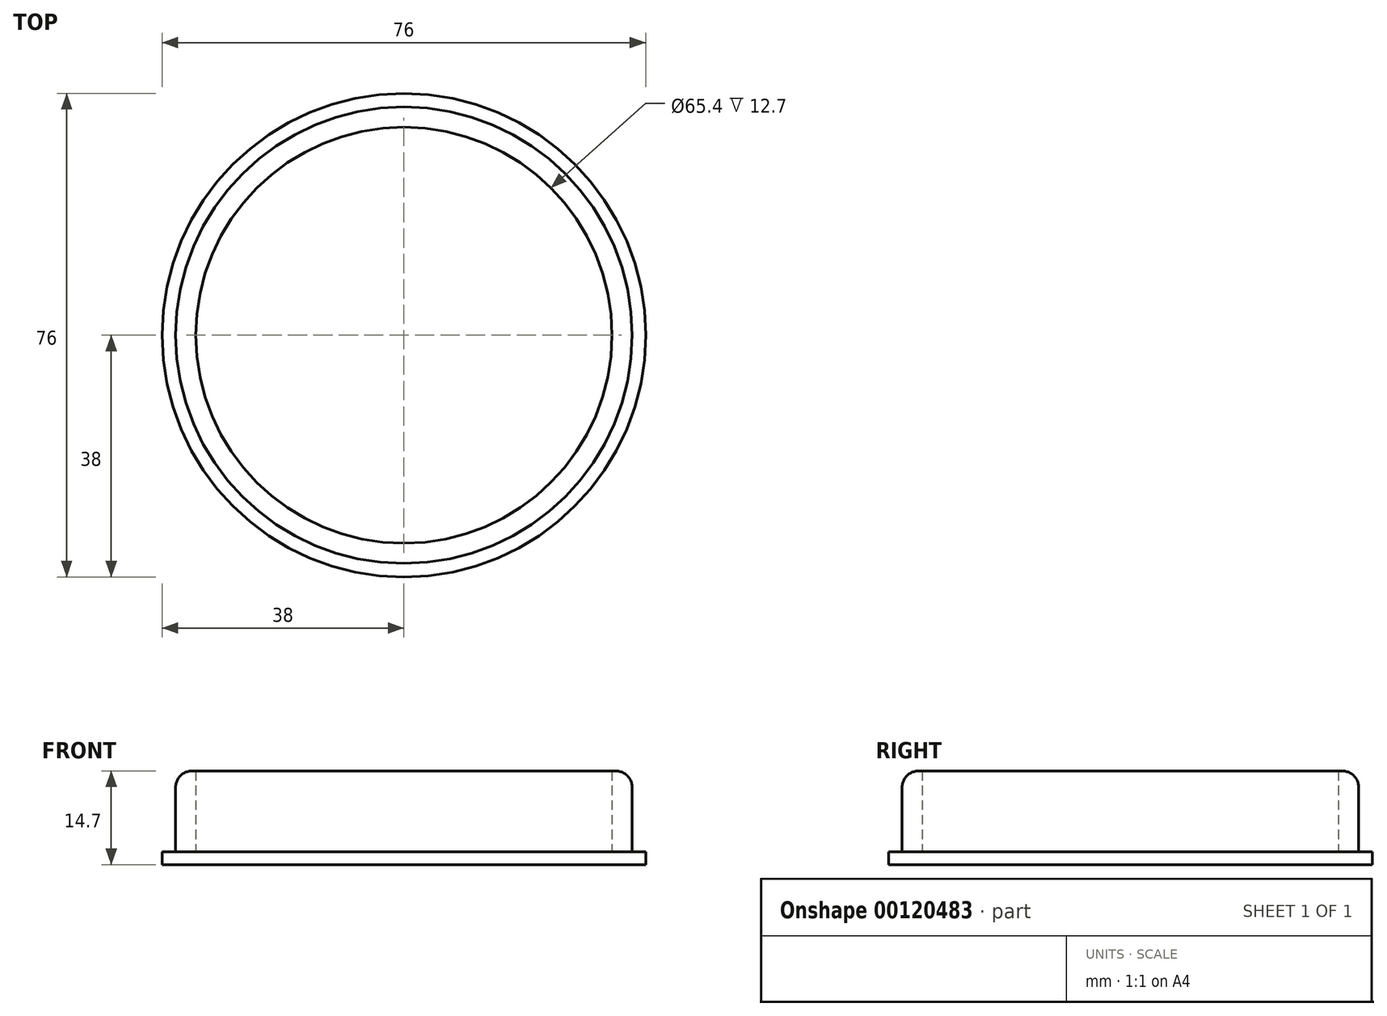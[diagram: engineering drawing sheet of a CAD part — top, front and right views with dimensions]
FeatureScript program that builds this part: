
annotation { "Feature Type Name" : "Feature", "Feature Type Description" : "" }
export const myFeature = defineFeature(function(context is Context, id is Id, definition is map)
    precondition{}
    {
        {
            var Q0;
            Q0=qCreatedBy(makeId("Top.planeOp"),FACE);
            var sketch = newSketch(context, id + "F0", { "sketchPlane" : qUnion([Q0])});
            skCircle(sketch, "E0", {"center": v(0, 0) * mm, "radius": 38 * mm});
            skSolve(sketch);
        }
        {
            var Q0;
            Q0=makeQuery(id+"F0.imprint","IMPRINT",FACE,{"disambiguationData":[TD([[makeQuery(id+"F0.imprint","IMPRINT",EDGE,{"derivedFrom":sQuery(id+"F0.wireOp",EDGE,"E0")}),1.0]])]});
            extrude(context, id + "F1", {"entities" : qUnion([Q0]), "depth" : 2 * mm});
        }
        {
            var Q0;
            Q0=makeQuery(id+"F1.opExtrude","CAP_FACE",FACE,{"disambiguationData":[OSD([sQuery(id+"F0.wireOp",EDGE,"E0")])],"isStart":false});
            var sketch = newSketch(context, id + "F2", { "sketchPlane" : qUnion([Q0])});
            skCircle(sketch, "E1", {"center": v(0, 0) * mm, "radius": 35.88 * mm});
            skCircle(sketch, "E2.0", {"center": v(0, 0) * mm, "radius": 32.7 * mm});
            skSolve(sketch);
        }
        {
            var Q0;
            Q0 = qSketchRegion(id + "F2", true);
            extrude(context, id + "F3", {"entities" : qUnion([Q0]), "operationType" : NewBodyOperationType.ADD, "depth" : 12.7 * mm});
        }
        {
            var Q0;
            Q0=makeQuery(id+"F3.opExtrude","CAP_EDGE",EDGE,{"disambiguationData":[OSD([sQuery(id+"F2.wireOp",EDGE,"E1")])],"isStart":false});
            fillet(context, id + "F4", {"entities" : qUnion([Q0]), "radius" : 2.54 * mm, "tangentPropagation" : true, "allowEdgeOverflow" : false});
        }
    });
